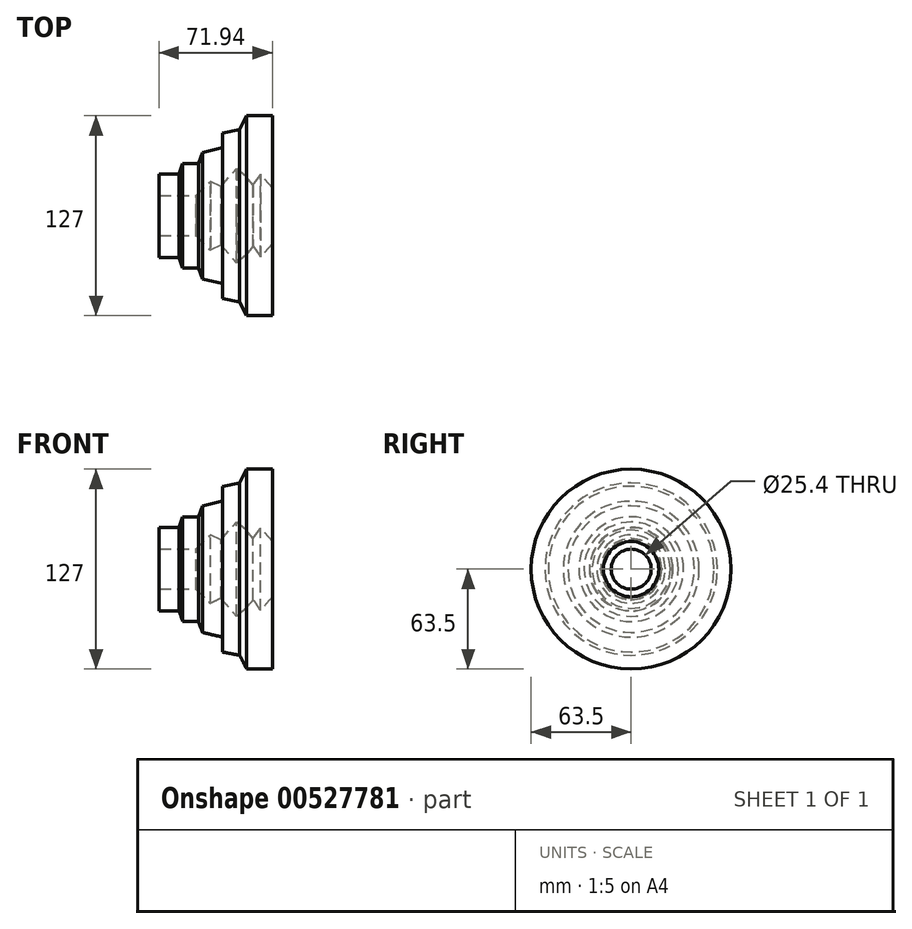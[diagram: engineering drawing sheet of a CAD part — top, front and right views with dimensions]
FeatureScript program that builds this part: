
annotation { "Feature Type Name" : "Feature", "Feature Type Description" : "" }
export const myFeature = defineFeature(function(context is Context, id is Id, definition is map)
    precondition{}
    {
        {
            var Q0;
            Q0=qCreatedBy(makeId("Front.planeOp"),FACE);
            var sketch = newSketch(context, id + "F0", { "sketchPlane" : qUnion([Q0])});
            skLineSegment(sketch, "E0", {"start": v(0, 0) * mm, "end": v(-119.78, 0) * mm});
            skLineSegment(sketch, "E1", {"start": v(0, 17.55) * mm, "end": v(0, 63.5) * mm});
            skLineSegment(sketch, "E2", {"start": v(0, 63.5) * mm, "end": v(-16.3, 63.5) * mm});
            skLineSegment(sketch, "E3", {"start": v(-16.3, 63.5) * mm, "end": v(-20.68, 54.73) * mm});
            skLineSegment(sketch, "E4", {"start": v(-20.68, 54.73) * mm, "end": v(-31.53, 52.65) * mm});
            skLineSegment(sketch, "E5", {"start": v(-31.53, 52.65) * mm, "end": v(-31.53, 43.18) * mm});
            skLineSegment(sketch, "E6", {"start": v(-31.53, 43.18) * mm, "end": v(-44.46, 40.18) * mm});
            skLineSegment(sketch, "E7", {"start": v(-44.46, 40.18) * mm, "end": v(-47, 33.25) * mm});
            skLineSegment(sketch, "E8", {"start": v(-47, 33.25) * mm, "end": v(-56.93, 33.25) * mm});
            skLineSegment(sketch, "E9", {"start": v(-56.93, 33.25) * mm, "end": v(-59.24, 26.55) * mm});
            skLineSegment(sketch, "E10", {"start": v(-59.24, 26.55) * mm, "end": v(-71.94, 26.55) * mm});
            skLineSegment(sketch, "E11", {"start": v(-71.94, 26.55) * mm, "end": v(-71.94, 12.7) * mm});
            skLineSegment(sketch, "E12", {"start": v(-71.94, 12.7) * mm, "end": v(-48.62, 12.7) * mm});
            skLineSegment(sketch, "E13", {"start": v(-48.62, 12.7) * mm, "end": v(-39.38, 21.7) * mm});
            skLineSegment(sketch, "E14", {"start": v(-39.38, 21.7) * mm, "end": v(-32.68, 18.47) * mm});
            skLineSegment(sketch, "E15", {"start": v(-32.68, 18.47) * mm, "end": v(-22.75, 29.95) * mm});
            skLineSegment(sketch, "E16", {"start": v(-22.75, 29.95) * mm, "end": v(-16.84, 24.84) * mm});
            skLineSegment(sketch, "E17", {"start": v(-16.84, 24.84) * mm, "end": v(-12.13, 19.4) * mm});
            skLineSegment(sketch, "E18", {"start": v(-12.13, 19.4) * mm, "end": v(-7.52, 26.32) * mm});
            skLineSegment(sketch, "E19", {"start": v(-7.52, 26.32) * mm, "end": v(0, 17.55) * mm});
            skSolve(sketch);
        }
        {
            var Q0;
            Q0=makeQuery(id+"F0.imprint","IMPRINT",FACE,{"disambiguationData":[TD([[makeQuery(id+"F0.imprint","IMPRINT",EDGE,{"derivedFrom":sQuery(id+"F0.wireOp",EDGE,"E1")}),1.0]])]});
            var Q1;
            Q1=sQuery(id+"F0.wireOp",EDGE,"E0");
            revolve(context, id + "F1", {"entities" : qUnion([Q0]), "axis" : qUnion([Q1]), "revolveType" : RevolveType.FULL});
        }
    });
